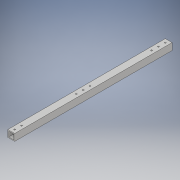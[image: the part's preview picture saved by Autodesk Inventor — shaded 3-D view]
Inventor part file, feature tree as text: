
AUTODESK INVENTOR PART (.ipt)
format: ipt  version: 2018 (Build 220112000, 112)  size: 132,608 bytes
history: native  units: in
note: dims shown in document units (in); Inventor stores cm internally (conversion verified against a paired STEP export)
features: extrude x2, sketch x2
ambient origin geometry x8: Origin, YZ Plane, XZ Plane, XY Plane, X Axis, Y Axis, Z Axis, Center Point
bodies: Solid1 (feature_tree)
feature tree (4):
  extrude  "Extrusion1"  Depth=1.0in
  extrude  "Extrusion2"  Depth=23.0in TaperAngle=0.0deg
  sketch  "Sketch1"  dims[d0=1.0in d1=1.0in]
  sketch  "Sketch3"  dims[d2=0.125in d3=23.0in d4=0.0in d5=11.0in d6=0.5in d7=1.0in d8=2.0in d9=0.5in d10=1.0in d11=0.5in d12=1.0in d13=1.0in d14=0.2031in d15=23.875in d16=0.0in]
